# Revit family: Outdoor Armor Water Heater OAN701-OAN801
name_source: partatom
category: Mechanical Equipment
revit_build: Autodesk Revit 2014 (Build: 20130308_1515(x64)
units: mm (PartAtom-declared; Revit-internal decimal feet)

## types (2) — shared parameters
# of Electrical Connections = 1
A_HEIGHT = 42 1/2"
D_ Drain Offset From Back = 23 1/4"
Description = Armor Outdoor Water Heater
FUEL TYPE = NATURAL GAS
F_ Water Outlet Offset from Back = 17 1/4"
Flue Radius = 3"
Fuel Type = Natural or LP
GAS CONN SIZE = 1"
G_Water Inlet Offset from Back = 3 1/2"
Gas Conn Radius = 1/2"
Manufacturer = Lochinvar
SES BIM Studio # = 16 0649 04-2
Total Amps = 1.5
URL = http://www.lochinvar.com
VENT SIZE = 6"
Voltage/Control = 24
Voltage/Heater = 120
WATER CONN SIZE = 2"
WIDTH = 15 1/2"
Water Conn Radius = 1"
Water Outlet Radius = 11 3/4"

## per-type parameters (varying)
| type | C_ DEPTH | Center of Flue | E_Condensate Drain Offset from Back | H_Gas Conn Offset from Back | H_Gas Conn Offset from Left | INPUT RATE (BTUH) | I_Gas Conn Height | J_Flue Depth | K_Flue Height |
| OAN701 | 41 1/4" | 9" | 29 1/4" | 3" | 3" | 700,000 | 32 3/4" | 12" | 49 1/2" |
| OAN801 | 43 1/4" | 9 1/4" | 33 1/2" | 3 1/2" | 3 1/4" | 800,000 | 33" | 12 1/4" | 50 1/2" |

note: column(s) folded — value = type name in every type: MODEL NO., Model

## geometry (parser evidence)
native form markers: Sweep x1
no freeform markers — native parametric forms only
